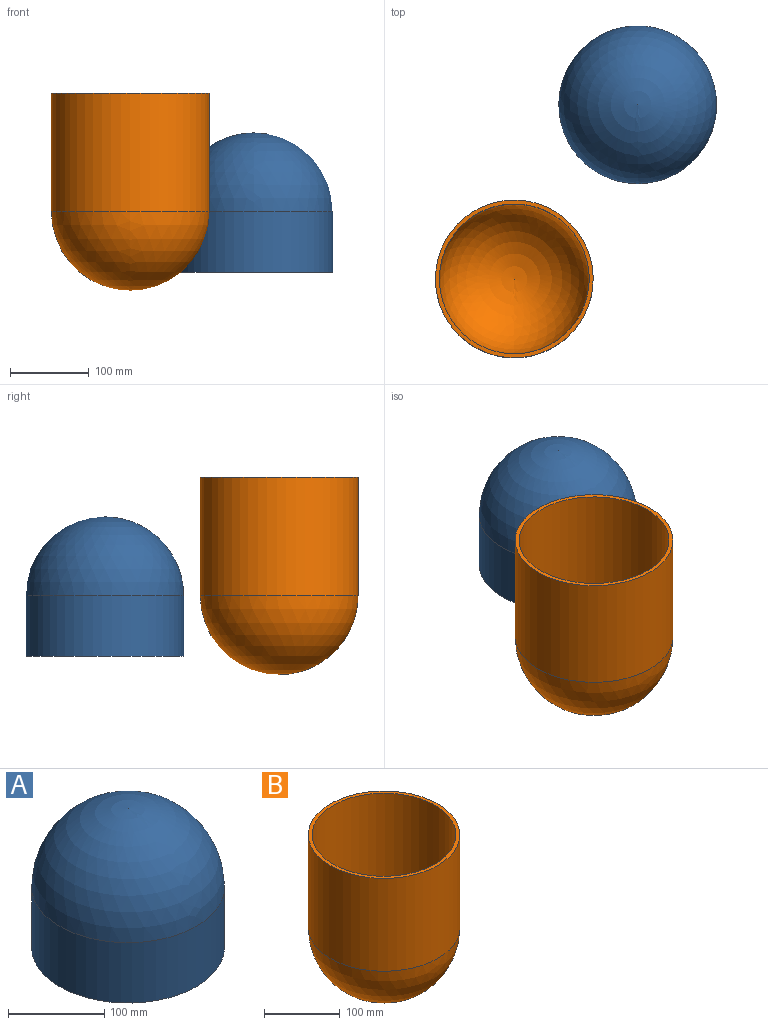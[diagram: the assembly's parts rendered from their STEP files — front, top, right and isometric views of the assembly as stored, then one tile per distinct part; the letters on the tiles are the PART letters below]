
ASSEMBLY  parts=2 mates=1
PART A: 3 faces, bbox 200x200x176.7 mm
  f0: sphere r=100mm, area 62831.9mm2, adj f1
  f1: cylinder r=100mm len=200mm, axis (0,0,1), area 48171.8mm2, adj f0,f2
  f2: plane 200x200mm, normal (0,0,-1), area 31415.9mm2, adj f1
PART B: 5 faces, bbox 200x200x250 mm
  f0: sphere r=95mm, area 56705.7mm2, adj f1
  f1: cylinder r=95mm len=190mm, axis (0,0,1), area 89535.4mm2, adj f0,f2
  f2: plane 200x200mm, normal (0,0,1), area 3063.1mm2, adj f1,f3
  f3: cylinder r=100mm len=200mm, axis (0,0,1), area 94247.8mm2, adj f2,f4
  f4: sphere r=100mm, area 62831.9mm2, adj f3
PLACE A t=(0,0,67.1)mm
PLACE B t=(-156.46,-221,-132.9)mm
MATE planar B.f1 <-> A.f1  axis (0,0,1) through (-156.46,-221,-132.9)mm
